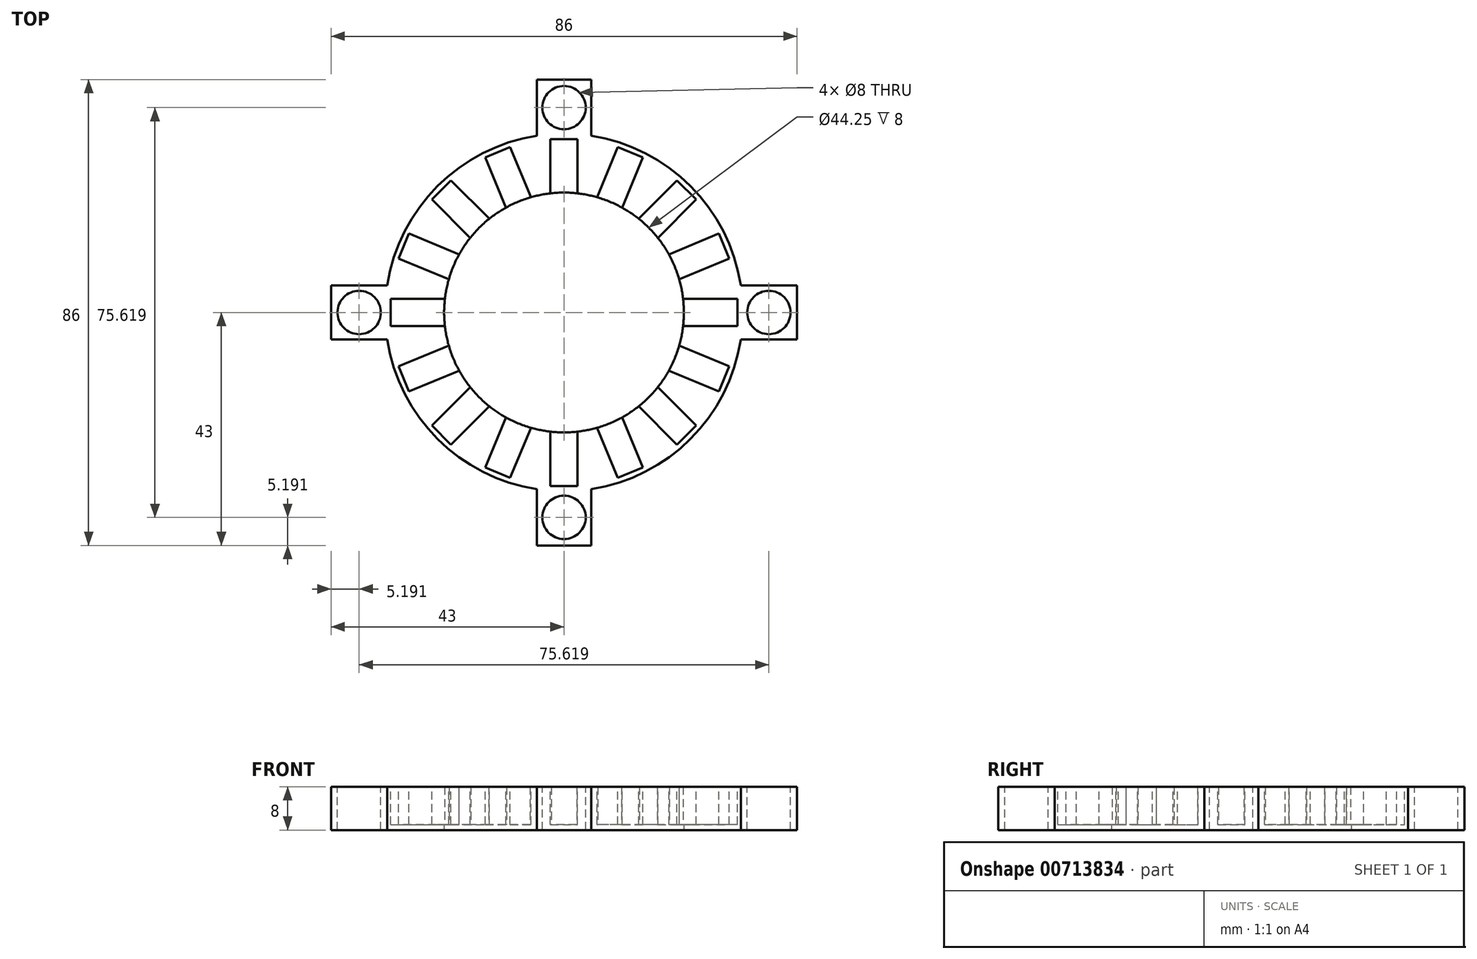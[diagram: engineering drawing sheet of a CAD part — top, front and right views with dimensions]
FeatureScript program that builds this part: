
annotation { "Feature Type Name" : "Feature", "Feature Type Description" : "" }
export const myFeature = defineFeature(function(context is Context, id is Id, definition is map)
    precondition{}
    {
        {
            var Q0;
            Q0=qCreatedBy(makeId("Front.planeOp"),FACE);
            var sketch = newSketch(context, id + "F0", { "sketchPlane" : qUnion([Q0])});
            skLineSegment(sketch, "E0", {"start": v(0, 0) * mm, "end": v(0, 8) * mm});
            skLineSegment(sketch, "E1", {"start": v(0, 8) * mm, "end": v(33, 8) * mm});
            skLineSegment(sketch, "E2", {"start": v(33, 8) * mm, "end": v(33, 0) * mm});
            skLineSegment(sketch, "E3", {"start": v(33, 0) * mm, "end": v(0, 0) * mm});
            skSolve(sketch);
        }
        {
            var Q0;
            Q0 = qSketchRegion(id + "F0", true);
            var Q1;
            Q1=sQuery(id+"F0.wireOp",EDGE,"E0");
            revolve(context, id + "F1", {"surfaceOperationType" : NewSurfaceOperationType.NEW, "entities" : qUnion([Q0]), "axis" : qUnion([Q1]), "revolveType" : RevolveType.FULL});
        }
        {
            var Q0;
            Q0=qCreatedBy(makeId("Top.planeOp"),FACE);
            var sketch = newSketch(context, id + "F2", { "sketchPlane" : qUnion([Q0])});
            skCircle(sketch, "E4", {"center": v(0, 0) * mm, "radius": 22.12 * mm});
            skSolve(sketch);
        }
        {
            var Q0;
            Q0 = qSketchRegion(id + "F2", true);
            extrude(context, id + "F3", {"entities" : qUnion([Q0]), "operationType" : NewBodyOperationType.REMOVE, "depth" : 25 * mm, "offsetDistance" : 25 * mm});
        }
        {
            var Q0;
            Q0=makeQuery(id+"F1.opRevolve","SWEPT_FACE",FACE,{"disambiguationData":[OSD([sQuery(id+"F0.wireOp",EDGE,"E1")])]});
            var sketch = newSketch(context, id + "F4", { "sketchPlane" : qUnion([Q0])});
            skLineSegment(sketch, "E5", {"start": v(0, 0) * mm, "end": v(0, 22) * mm});
            skLineSegment(sketch, "E6", {"start": v(0, 22) * mm, "end": v(-2.5, 22) * mm});
            skLineSegment(sketch, "E7", {"start": v(-2.5, 22) * mm, "end": v(-2.5, 32) * mm});
            skLineSegment(sketch, "E8", {"start": v(-2.5, 32) * mm, "end": v(2.5, 32) * mm});
            skLineSegment(sketch, "E9", {"start": v(2.5, 32) * mm, "end": v(2.5, 22) * mm});
            skLineSegment(sketch, "E10", {"start": v(2.5, 22) * mm, "end": v(0, 22) * mm});
            skLineSegment(sketch, "E11.1.0", {"start": v(-10.73, 19.37) * mm, "end": v(-14.56, 28.6) * mm});
            skLineSegment(sketch, "E11.1.1", {"start": v(-14.56, 28.6) * mm, "end": v(-9.94, 30.52) * mm});
            skLineSegment(sketch, "E11.1.2", {"start": v(-9.94, 30.52) * mm, "end": v(-6.1, 21.28) * mm});
            skLineSegment(sketch, "E11.1.3", {"start": v(-6.1, 21.28) * mm, "end": v(-8.42, 20.33) * mm});
            skLineSegment(sketch, "E11.1.4", {"start": v(-8.42, 20.33) * mm, "end": v(-10.73, 19.37) * mm});
            skLineSegment(sketch, "E11.2.0", {"start": v(-17.32, 13.79) * mm, "end": v(-24.4, 20.86) * mm});
            skLineSegment(sketch, "E11.2.1", {"start": v(-24.4, 20.86) * mm, "end": v(-20.86, 24.4) * mm});
            skLineSegment(sketch, "E11.2.2", {"start": v(-20.86, 24.4) * mm, "end": v(-13.79, 17.32) * mm});
            skLineSegment(sketch, "E11.2.3", {"start": v(-13.79, 17.32) * mm, "end": v(-15.56, 15.56) * mm});
            skLineSegment(sketch, "E11.2.4", {"start": v(-15.56, 15.56) * mm, "end": v(-17.32, 13.79) * mm});
            skPoint(sketch, "E11.center", {"position": v(0, 0) * mm});
            skLineSegment(sketch, "E12.1.3.0", {"start": v(-21.28, 6.1) * mm, "end": v(-30.52, 9.94) * mm});
            skLineSegment(sketch, "E12.3.3.0", {"start": v(-30.52, 9.94) * mm, "end": v(-28.6, 14.56) * mm});
            skLineSegment(sketch, "E12.6.3.0", {"start": v(-28.6, 14.56) * mm, "end": v(-19.37, 10.73) * mm});
            skLineSegment(sketch, "E12.9.3.0", {"start": v(-19.37, 10.73) * mm, "end": v(-20.33, 8.42) * mm});
            skLineSegment(sketch, "E12.12.3.0", {"start": v(-20.33, 8.42) * mm, "end": v(-21.28, 6.1) * mm});
            skLineSegment(sketch, "E12.1.4.0", {"start": v(-22, -2.5) * mm, "end": v(-32, -2.5) * mm});
            skLineSegment(sketch, "E12.3.4.0", {"start": v(-32, -2.5) * mm, "end": v(-32, 2.5) * mm});
            skLineSegment(sketch, "E12.6.4.0", {"start": v(-32, 2.5) * mm, "end": v(-22, 2.5) * mm});
            skLineSegment(sketch, "E12.9.4.0", {"start": v(-22, 2.5) * mm, "end": v(-22, 0) * mm});
            skLineSegment(sketch, "E12.12.4.0", {"start": v(-22, 0) * mm, "end": v(-22, -2.5) * mm});
            skLineSegment(sketch, "E12.1.5.0", {"start": v(-19.37, -10.73) * mm, "end": v(-28.6, -14.56) * mm});
            skLineSegment(sketch, "E12.3.5.0", {"start": v(-28.6, -14.56) * mm, "end": v(-30.52, -9.94) * mm});
            skLineSegment(sketch, "E12.6.5.0", {"start": v(-30.52, -9.94) * mm, "end": v(-21.28, -6.1) * mm});
            skLineSegment(sketch, "E12.9.5.0", {"start": v(-21.28, -6.1) * mm, "end": v(-20.33, -8.42) * mm});
            skLineSegment(sketch, "E12.12.5.0", {"start": v(-20.33, -8.42) * mm, "end": v(-19.37, -10.73) * mm});
            skLineSegment(sketch, "E12.1.6.0", {"start": v(-13.79, -17.32) * mm, "end": v(-20.86, -24.4) * mm});
            skLineSegment(sketch, "E12.3.6.0", {"start": v(-20.86, -24.4) * mm, "end": v(-24.4, -20.86) * mm});
            skLineSegment(sketch, "E12.6.6.0", {"start": v(-24.4, -20.86) * mm, "end": v(-17.32, -13.79) * mm});
            skLineSegment(sketch, "E12.9.6.0", {"start": v(-17.32, -13.79) * mm, "end": v(-15.56, -15.56) * mm});
            skLineSegment(sketch, "E12.12.6.0", {"start": v(-15.56, -15.56) * mm, "end": v(-13.79, -17.32) * mm});
            skLineSegment(sketch, "E12.1.7.0", {"start": v(-6.1, -21.28) * mm, "end": v(-9.94, -30.52) * mm});
            skLineSegment(sketch, "E12.3.7.0", {"start": v(-9.94, -30.52) * mm, "end": v(-14.56, -28.6) * mm});
            skLineSegment(sketch, "E12.6.7.0", {"start": v(-14.56, -28.6) * mm, "end": v(-10.73, -19.37) * mm});
            skLineSegment(sketch, "E12.9.7.0", {"start": v(-10.73, -19.37) * mm, "end": v(-8.42, -20.33) * mm});
            skLineSegment(sketch, "E12.12.7.0", {"start": v(-8.42, -20.33) * mm, "end": v(-6.1, -21.28) * mm});
            skLineSegment(sketch, "E12.1.8.0", {"start": v(2.5, -22) * mm, "end": v(2.5, -32) * mm});
            skLineSegment(sketch, "E12.3.8.0", {"start": v(2.5, -32) * mm, "end": v(-2.5, -32) * mm});
            skLineSegment(sketch, "E12.6.8.0", {"start": v(-2.5, -32) * mm, "end": v(-2.5, -22) * mm});
            skLineSegment(sketch, "E12.9.8.0", {"start": v(-2.5, -22) * mm, "end": v(0, -22) * mm});
            skLineSegment(sketch, "E12.12.8.0", {"start": v(0, -22) * mm, "end": v(2.5, -22) * mm});
            skLineSegment(sketch, "E12.1.9.0", {"start": v(10.73, -19.37) * mm, "end": v(14.56, -28.6) * mm});
            skLineSegment(sketch, "E12.3.9.0", {"start": v(14.56, -28.6) * mm, "end": v(9.94, -30.52) * mm});
            skLineSegment(sketch, "E12.6.9.0", {"start": v(9.94, -30.52) * mm, "end": v(6.1, -21.28) * mm});
            skLineSegment(sketch, "E12.9.9.0", {"start": v(6.1, -21.28) * mm, "end": v(8.42, -20.33) * mm});
            skLineSegment(sketch, "E12.12.9.0", {"start": v(8.42, -20.33) * mm, "end": v(10.73, -19.37) * mm});
            skLineSegment(sketch, "E12.1.10.0", {"start": v(17.32, -13.79) * mm, "end": v(24.4, -20.86) * mm});
            skLineSegment(sketch, "E12.3.10.0", {"start": v(24.4, -20.86) * mm, "end": v(20.86, -24.4) * mm});
            skLineSegment(sketch, "E12.6.10.0", {"start": v(20.86, -24.4) * mm, "end": v(13.79, -17.32) * mm});
            skLineSegment(sketch, "E12.9.10.0", {"start": v(13.79, -17.32) * mm, "end": v(15.56, -15.56) * mm});
            skLineSegment(sketch, "E12.12.10.0", {"start": v(15.56, -15.56) * mm, "end": v(17.32, -13.79) * mm});
            skLineSegment(sketch, "E12.1.11.0", {"start": v(21.28, -6.1) * mm, "end": v(30.52, -9.94) * mm});
            skLineSegment(sketch, "E12.3.11.0", {"start": v(30.52, -9.94) * mm, "end": v(28.6, -14.56) * mm});
            skLineSegment(sketch, "E12.6.11.0", {"start": v(28.6, -14.56) * mm, "end": v(19.37, -10.73) * mm});
            skLineSegment(sketch, "E12.9.11.0", {"start": v(19.37, -10.73) * mm, "end": v(20.33, -8.42) * mm});
            skLineSegment(sketch, "E12.12.11.0", {"start": v(20.33, -8.42) * mm, "end": v(21.28, -6.1) * mm});
            skLineSegment(sketch, "E12.1.12.0", {"start": v(22, 2.5) * mm, "end": v(32, 2.5) * mm});
            skLineSegment(sketch, "E12.3.12.0", {"start": v(32, 2.5) * mm, "end": v(32, -2.5) * mm});
            skLineSegment(sketch, "E12.6.12.0", {"start": v(32, -2.5) * mm, "end": v(22, -2.5) * mm});
            skLineSegment(sketch, "E12.9.12.0", {"start": v(22, -2.5) * mm, "end": v(22, 0) * mm});
            skLineSegment(sketch, "E12.12.12.0", {"start": v(22, 0) * mm, "end": v(22, 2.5) * mm});
            skLineSegment(sketch, "E12.1.13.0", {"start": v(19.37, 10.73) * mm, "end": v(28.6, 14.56) * mm});
            skLineSegment(sketch, "E12.3.13.0", {"start": v(28.6, 14.56) * mm, "end": v(30.52, 9.94) * mm});
            skLineSegment(sketch, "E12.6.13.0", {"start": v(30.52, 9.94) * mm, "end": v(21.28, 6.1) * mm});
            skLineSegment(sketch, "E12.9.13.0", {"start": v(21.28, 6.1) * mm, "end": v(20.33, 8.42) * mm});
            skLineSegment(sketch, "E12.12.13.0", {"start": v(20.33, 8.42) * mm, "end": v(19.37, 10.73) * mm});
            skLineSegment(sketch, "E12.1.14.0", {"start": v(13.79, 17.32) * mm, "end": v(20.86, 24.4) * mm});
            skLineSegment(sketch, "E12.3.14.0", {"start": v(20.86, 24.4) * mm, "end": v(24.4, 20.86) * mm});
            skLineSegment(sketch, "E12.6.14.0", {"start": v(24.4, 20.86) * mm, "end": v(17.32, 13.79) * mm});
            skLineSegment(sketch, "E12.9.14.0", {"start": v(17.32, 13.79) * mm, "end": v(15.56, 15.56) * mm});
            skLineSegment(sketch, "E12.12.14.0", {"start": v(15.56, 15.56) * mm, "end": v(13.79, 17.32) * mm});
            skLineSegment(sketch, "E12.1.15.0", {"start": v(6.1, 21.28) * mm, "end": v(9.94, 30.52) * mm});
            skLineSegment(sketch, "E12.3.15.0", {"start": v(9.94, 30.52) * mm, "end": v(14.56, 28.6) * mm});
            skLineSegment(sketch, "E12.6.15.0", {"start": v(14.56, 28.6) * mm, "end": v(10.73, 19.37) * mm});
            skLineSegment(sketch, "E12.9.15.0", {"start": v(10.73, 19.37) * mm, "end": v(8.42, 20.33) * mm});
            skLineSegment(sketch, "E12.12.15.0", {"start": v(8.42, 20.33) * mm, "end": v(6.1, 21.28) * mm});
            skSolve(sketch);
        }
        {
            var Q0;
            Q0 = qSketchRegion(id + "F4", true);
            extrude(context, id + "F5", {"entities" : qUnion([Q0]), "operationType" : NewBodyOperationType.REMOVE, "oppositeDirection" : true, "depth" : 7 * mm, "offsetDistance" : 25 * mm});
        }
        {
            var Q0;
            Q0=qCreatedBy(makeId("Top.planeOp"),FACE);
            var sketch = newSketch(context, id + "F6", { "sketchPlane" : qUnion([Q0])});
            skLineSegment(sketch, "E13", {"start": v(0, 0) * mm, "end": v(0, 8) * mm});
            skLineSegment(sketch, "E14", {"start": v(43, 0) * mm, "end": v(43, -5) * mm});
            skLineSegment(sketch, "E15", {"start": v(43, -5) * mm, "end": v(32.62, -5) * mm});
            skLineSegment(sketch, "E16", {"start": v(43, 0) * mm, "end": v(43, 5) * mm});
            skLineSegment(sketch, "E17", {"start": v(43, 5) * mm, "end": v(32.62, 5) * mm});
            skLineSegment(sketch, "E18.1.0", {"start": v(5, 43) * mm, "end": v(5, 32.62) * mm});
            skLineSegment(sketch, "E18.1.1", {"start": v(0, 43) * mm, "end": v(5, 43) * mm});
            skLineSegment(sketch, "E18.1.2", {"start": v(0, 43) * mm, "end": v(-5, 43) * mm});
            skLineSegment(sketch, "E18.1.3", {"start": v(-5, 43) * mm, "end": v(-5, 32.62) * mm});
            skLineSegment(sketch, "E18.2.0", {"start": v(-43, 5) * mm, "end": v(-32.62, 5) * mm});
            skLineSegment(sketch, "E18.2.1", {"start": v(-43, 0) * mm, "end": v(-43, 5) * mm});
            skLineSegment(sketch, "E18.2.2", {"start": v(-43, 0) * mm, "end": v(-43, -5) * mm});
            skLineSegment(sketch, "E18.2.3", {"start": v(-43, -5) * mm, "end": v(-32.62, -5) * mm});
            skLineSegment(sketch, "E18.3.0", {"start": v(-5, -43) * mm, "end": v(-5, -32.62) * mm});
            skLineSegment(sketch, "E18.3.1", {"start": v(0, -43) * mm, "end": v(-5, -43) * mm});
            skLineSegment(sketch, "E18.3.2", {"start": v(0, -43) * mm, "end": v(5, -43) * mm});
            skLineSegment(sketch, "E18.3.3", {"start": v(5, -43) * mm, "end": v(5, -32.62) * mm});
            skPoint(sketch, "E18.center", {"position": v(0, 0) * mm});
            skLineSegment(sketch, "E19", {"start": v(32.62, 5) * mm, "end": v(32.62, -5) * mm});
            skLineSegment(sketch, "E20", {"start": v(5, 32.62) * mm, "end": v(-5, 32.62) * mm});
            skLineSegment(sketch, "E21", {"start": v(-32.62, 5) * mm, "end": v(-32.62, -5) * mm});
            skLineSegment(sketch, "E22", {"start": v(-5, -32.62) * mm, "end": v(5, -32.62) * mm});
            skSolve(sketch);
        }
        {
            var Q0;
            Q0 = qSketchRegion(id + "F6", true);
            extrude(context, id + "F7", {"entities" : qUnion([Q0]), "operationType" : NewBodyOperationType.ADD, "depth" : 8 * mm, "offsetDistance" : 25 * mm});
        }
        {
            var Q0;
            Q0=makeQuery(id+"F7.boolean.opBoolean","MERGE",FACE,{"derivedFrom":[makeQuery(id+"F1.opRevolve","SWEPT_FACE",FACE,{"disambiguationData":[OSD([sQuery(id+"F0.wireOp",EDGE,"E1")])]}),makeQuery(id+"F7.opExtrude","CAP_FACE",FACE,{"disambiguationData":[OSD([sQuery(id+"F6.wireOp",EDGE,"E14"),sQuery(id+"F6.wireOp",EDGE,"E15"),sQuery(id+"F6.wireOp",EDGE,"E16"),sQuery(id+"F6.wireOp",EDGE,"E17"),sQuery(id+"F6.wireOp",EDGE,"E19")])],"isStart":false}),makeQuery(id+"F7.opExtrude","CAP_FACE",FACE,{"disambiguationData":[OSD([sQuery(id+"F6.wireOp",EDGE,"E18.1.0"),sQuery(id+"F6.wireOp",EDGE,"E18.1.1"),sQuery(id+"F6.wireOp",EDGE,"E18.1.2"),sQuery(id+"F6.wireOp",EDGE,"E18.1.3"),sQuery(id+"F6.wireOp",EDGE,"E20")])],"isStart":false}),makeQuery(id+"F7.opExtrude","CAP_FACE",FACE,{"disambiguationData":[OSD([sQuery(id+"F6.wireOp",EDGE,"E18.2.0"),sQuery(id+"F6.wireOp",EDGE,"E18.2.1"),sQuery(id+"F6.wireOp",EDGE,"E18.2.2"),sQuery(id+"F6.wireOp",EDGE,"E18.2.3"),sQuery(id+"F6.wireOp",EDGE,"E21")])],"isStart":false}),makeQuery(id+"F7.opExtrude","CAP_FACE",FACE,{"disambiguationData":[OSD([sQuery(id+"F6.wireOp",EDGE,"E18.3.0"),sQuery(id+"F6.wireOp",EDGE,"E18.3.1"),sQuery(id+"F6.wireOp",EDGE,"E18.3.2"),sQuery(id+"F6.wireOp",EDGE,"E18.3.3"),sQuery(id+"F6.wireOp",EDGE,"E22")])],"isStart":false})]});
            var sketch = newSketch(context, id + "F8", { "sketchPlane" : qUnion([Q0])});
            skPoint(sketch, "E23", {"position": v(0, 38.1) * mm});
            skPoint(sketch, "E24", {"position": v(37.8, 0) * mm});
            skPoint(sketch, "E24.positionSnap0", {"position": v(37.8, 5) * mm});
            skCircle(sketch, "E25", {"center": v(37.8, 0) * mm, "radius": 4 * mm});
            skCircle(sketch, "E26.1.0", {"center": v(0, 37.8) * mm, "radius": 4 * mm});
            skCircle(sketch, "E26.2.0", {"center": v(-37.8, 0) * mm, "radius": 4 * mm});
            skCircle(sketch, "E26.3.0", {"center": v(0, -37.8) * mm, "radius": 4 * mm});
            skPoint(sketch, "E26.center", {"position": v(0, 0) * mm});
            skSolve(sketch);
        }
        {
            var Q0;
            Q0=makeQuery(id+"F8.imprint","IMPRINT",FACE,{"disambiguationData":[TD([[makeQuery(id+"F8.imprint","IMPRINT",EDGE,{"derivedFrom":sQuery(id+"F8.wireOp",EDGE,"E26.1.0")}),1.0]])]});
            var Q1;
            Q1=makeQuery(id+"F8.imprint","IMPRINT",FACE,{"disambiguationData":[TD([[makeQuery(id+"F8.imprint","IMPRINT",EDGE,{"derivedFrom":sQuery(id+"F8.wireOp",EDGE,"E25")}),1.0]])]});
            var Q2;
            Q2=makeQuery(id+"F8.imprint","IMPRINT",FACE,{"disambiguationData":[TD([[makeQuery(id+"F8.imprint","IMPRINT",EDGE,{"derivedFrom":sQuery(id+"F8.wireOp",EDGE,"E26.2.0")}),1.0]])]});
            var Q3;
            Q3=makeQuery(id+"F8.imprint","IMPRINT",FACE,{"disambiguationData":[TD([[makeQuery(id+"F8.imprint","IMPRINT",EDGE,{"derivedFrom":sQuery(id+"F8.wireOp",EDGE,"E26.3.0")}),1.0]])]});
            extrude(context, id + "F9", {"entities" : qUnion([Q0, Q1, Q2, Q3]), "operationType" : NewBodyOperationType.REMOVE, "oppositeDirection" : true, "depth" : 25 * mm, "offsetDistance" : 25 * mm});
        }
    });
